# Revit family: Soap_Dispenser-Deck_Mounted-Bobrick-SureFlo_B-828
name_source: partatom
category: Specialty Equipment
units: mm (PartAtom-declared; Revit-internal decimal feet)

## family parameters
Always vertical = No
Cut with Voids When Loaded = No
OmniClass Number = 23.40.20.21.34
OmniClass Title = Soap Holders, Dispensers
Part Type = Normal
Room Calculation Point = No
Round Connector Dimension = Use Diameter
Shared = Yes
Work Plane-Based = Yes

## types (1)
- B-828
    ADA Compliant = Yes
    ATS URL = http://www.atsspec.net
    Assembly Code = C1030210
    Default Elevation = 0"
    Description = SureFlo® Automatic Counter-Mounted Foam Soap Dispenser
    Finish = ABS Plastic-Bobrick-Chrome Plated
    Height = 2 15/16"
    Installation Instruction Link = http://www.bobrick.com
    Installation Type = Deck Mounted
    Length = 6 3/4"
    Manufacturer = Bobrick
    Masterformat Number = 10 28 16.13
    Masterformat Title = Residential Bath Accessories
    Material = ABS Plastic-Bobrick-White
    Model = B-828
    Omniclass Table 23 Code = 23.40.20.21.34
    Omniclass Table 23 Title = Soap Holders, Dispensers
    Operation = Unit is designed for installation into counter up to 2" (50mm) maximum thickness with minimum 1-3/8" (35mm) diameter mounting hole. Unit may be mounted through special hole requisitioned when lavatory is ordered from manufacturer (specify punching locations). Recommended mounting location is between 6" to 8" (150 to 205mm) from back wall and 3" (75mm) from the sink rim to the center of the mounting hole. Minimum 18" (455mm) vertical and 5" (125mm) diameter clearance required for soap bottle and bottom housing below mounting hole. Mount Battery Pack (mounting hardware located inside Battery Pack) on back or side wall in a convenient location nearest dispenser for ease of access to replace batteries. Install 4 “D” cell batteries (not included) in battery pack and plug in power cord into bottom motor housing. Designers Note: For sinks with rim over the counter area, ensure that rim does not come in contact with activation area. Please refer to 828-191 Installation Instruction.
    Price = Prices may vary. Please consult Manufacturer Representative for most up-to-date price list.
    Product Documentation Link = http://www.bobrick.com
    Product URL = http://www.bobrick.com
    Revised Date = 11/11/2020
    Specification = Automatic, Counter-Mounted Foam Soap Dispenser shall dispense adjustable amount (5 ml to 19 ml) of commercially marketed all-purpose bulk foam hand soaps. Spout assembly shall be bright polished chrome plated ABS plastic with integral shank to accommodate up to 2" (50mm) thick counter tops. Unit shall be equipped with oversized funnel shape opening, covered by a 180° rotatable lid with concealed locking mechanism to allow for top filling. Unit shall have LED indicators to show unit has been activated low battery life. Unit shall have IR Sensor located on PC board housed in a water-resistant plastic housing. Activation Lens shall allow for defined activation range to eliminate chance of false activation during hand washing. Unit equipped with unique two stage foam mixing chambers. Air pump delivers air to foam mixer housing, combining foam soap solution and air to form a preliminary mixture of foam. Soap is then pumped through spout where a second chamber in the nozzle tip which houses a mixer cartridge with Nylon mesh ultrasonically welded on both ends delivers a rich lather of foam soap. Portion Control Knob shall allow field adjustment of desired volume of soap dispensed per hand wash with an adjustment range of approximately .4ml to 1ml of liquid foam soap converted to 13ml to 15ml of foam dispensed into palm of hand. Unit shall be equipped with an Automatic System Flush Button to allow for cleaning and maintenance. Battery Pack uses 4 “D” cell batteries (not included) providing a battery life of up to 100,000 cycles or 2 years. Optional A/C adapter available, order Part No. 3974-57.
    URL = http://www.bobrick.com
    Warranty Information = 3 Years Limited Warranty
    Width = 2 3/4"

## geometry (parser evidence)
native form markers: Sweep x2
no freeform markers — native parametric forms only
